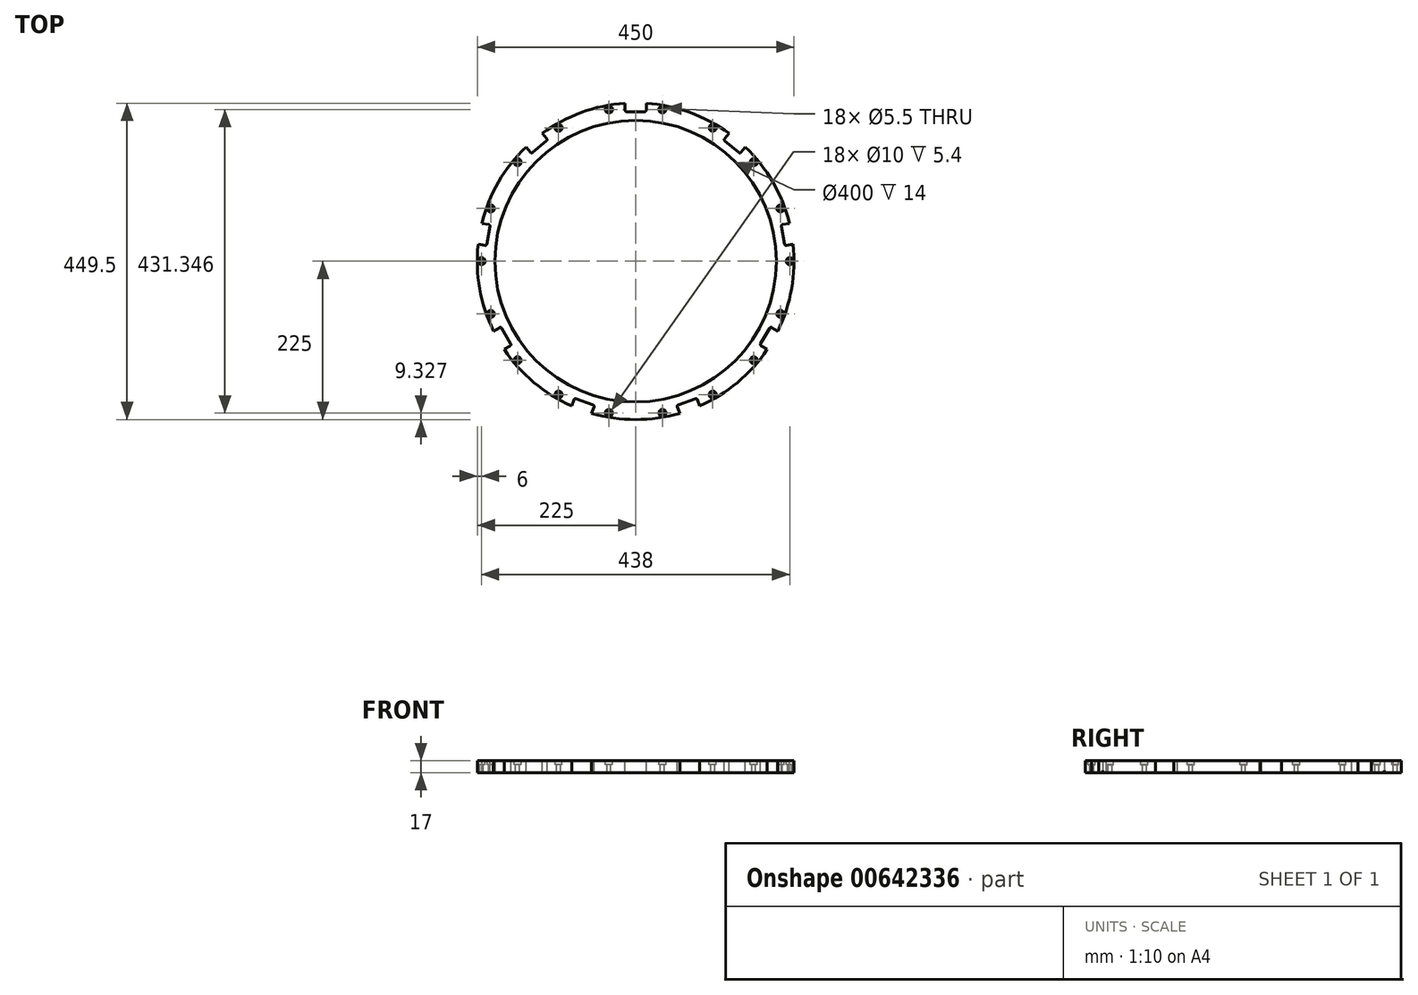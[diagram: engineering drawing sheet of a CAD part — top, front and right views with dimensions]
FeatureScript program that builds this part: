
annotation { "Feature Type Name" : "Feature", "Feature Type Description" : "" }
export const myFeature = defineFeature(function(context is Context, id is Id, definition is map)
    precondition{}
    {
        {
            var Q0;
            Q0=qCreatedBy(makeId("Top.planeOp"),FACE);
            var sketch = newSketch(context, id + "F0", { "sketchPlane" : qUnion([Q0])});
            skCircle(sketch, "E0", {"center": v(0, 0) * mm, "radius": 200 * mm});
            skCircle(sketch, "E1", {"center": v(0, 0) * mm, "radius": 225 * mm});
            skSolve(sketch);
        }
        {
            var Q0;
            Q0=makeQuery(id+"F0.imprint","IMPRINT",FACE,{"disambiguationData":[TD([[makeQuery(id+"F0.imprint","IMPRINT",EDGE,{"derivedFrom":sQuery(id+"F0.wireOp",EDGE,"E0")}),-1.0]])]});
            extrude(context, id + "F1", {"entities" : qUnion([Q0]), "depth" : 17 * mm, "offsetDistance" : 25 * mm});
        }
        {
            var Q0;
            Q0=makeQuery(id+"F1.opExtrude","CAP_FACE",FACE,{"disambiguationData":[OSD([sQuery(id+"F0.wireOp",EDGE,"E0"),sQuery(id+"F0.wireOp",EDGE,"E1")])],"isStart":false});
            var sketch = newSketch(context, id + "F2", { "sketchPlane" : qUnion([Q0])});
            skPoint(sketch, "E2", {"position": v(219, 0) * mm});
            skPoint(sketch, "E3.1.0", {"position": v(205.8, 74.9) * mm});
            skPoint(sketch, "E3.2.0", {"position": v(167.76, 140.77) * mm});
            skPoint(sketch, "E3.3.0", {"position": v(109.5, 189.66) * mm});
            skPoint(sketch, "E3.4.0", {"position": v(38.03, 215.67) * mm});
            skPoint(sketch, "E3.5.0", {"position": v(-38.03, 215.67) * mm});
            skPoint(sketch, "E3.6.0", {"position": v(-109.5, 189.66) * mm});
            skPoint(sketch, "E3.7.0", {"position": v(-167.76, 140.77) * mm});
            skPoint(sketch, "E3.8.0", {"position": v(-205.8, 74.9) * mm});
            skPoint(sketch, "E3.9.0", {"position": v(-219, 0) * mm});
            skPoint(sketch, "E3.10.0", {"position": v(-205.8, -74.9) * mm});
            skPoint(sketch, "E3.11.0", {"position": v(-167.76, -140.77) * mm});
            skPoint(sketch, "E3.12.0", {"position": v(-109.5, -189.66) * mm});
            skPoint(sketch, "E3.13.0", {"position": v(-38.03, -215.67) * mm});
            skPoint(sketch, "E3.14.0", {"position": v(38.03, -215.67) * mm});
            skPoint(sketch, "E3.15.0", {"position": v(109.5, -189.66) * mm});
            skPoint(sketch, "E3.16.0", {"position": v(167.76, -140.77) * mm});
            skPoint(sketch, "E3.17.0", {"position": v(205.8, -74.9) * mm});
            skPoint(sketch, "E3.center", {"position": v(0, 0) * mm});
            skSolve(sketch);
        }
        {
            var Q0;
            Q0=sQuery(id+"F2.wireOp",VERTEX,"E2");
            var Q1;
            Q1=sQuery(id+"F2.wireOp",VERTEX,"E3.1.0");
            var Q2;
            Q2=sQuery(id+"F2.wireOp",VERTEX,"E3.2.0");
            var Q3;
            Q3=sQuery(id+"F2.wireOp",VERTEX,"E3.3.0");
            var Q4;
            Q4=sQuery(id+"F2.wireOp",VERTEX,"E3.4.0");
            var Q5;
            Q5=sQuery(id+"F2.wireOp",VERTEX,"E3.5.0");
            var Q6;
            Q6=sQuery(id+"F2.wireOp",VERTEX,"E3.6.0");
            var Q7;
            Q7=sQuery(id+"F2.wireOp",VERTEX,"E3.7.0");
            var Q8;
            Q8=sQuery(id+"F2.wireOp",VERTEX,"E3.8.0");
            var Q9;
            Q9=sQuery(id+"F2.wireOp",VERTEX,"E3.9.0");
            var Q10;
            Q10=sQuery(id+"F2.wireOp",VERTEX,"E3.10.0");
            var Q11;
            Q11=sQuery(id+"F2.wireOp",VERTEX,"E3.11.0");
            var Q12;
            Q12=sQuery(id+"F2.wireOp",VERTEX,"E3.12.0");
            var Q13;
            Q13=sQuery(id+"F2.wireOp",VERTEX,"E3.13.0");
            var Q14;
            Q14=sQuery(id+"F2.wireOp",VERTEX,"E3.14.0");
            var Q15;
            Q15=sQuery(id+"F2.wireOp",VERTEX,"E3.15.0");
            var Q16;
            Q16=sQuery(id+"F2.wireOp",VERTEX,"E3.16.0");
            var Q17;
            Q17=sQuery(id+"F2.wireOp",VERTEX,"E3.17.0");
            var Q18;
            Q18=sQuery(id+"F2.wireOp",VERTEX,"E3.18.0");
            var Q19;
            Q19=sQuery(id+"F2.wireOp",VERTEX,"E3.19.0");
            var Q20;
            Q20=sQuery(id+"F2.wireOp",VERTEX,"E3.20.0");
            var Q21;
            Q21=sQuery(id+"F2.wireOp",VERTEX,"E3.21.0");
            var Q22;
            Q22=sQuery(id+"F2.wireOp",VERTEX,"E3.22.0");
            var Q23;
            Q23=sQuery(id+"F2.wireOp",VERTEX,"E3.23.0");
            var Q24;
            Q24=sQuery(id+"F2.wireOp",VERTEX,"E3.24.0");
            var Q25;
            Q25=sQuery(id+"F2.wireOp",VERTEX,"E3.25.0");
            var Q26;
            Q26=sQuery(id+"F2.wireOp",VERTEX,"E3.26.0");
            var Q27;
            Q27=sQuery(id+"F2.wireOp",VERTEX,"E3.27.0");
            var Q28;
            Q28=sQuery(id+"F2.wireOp",VERTEX,"E3.28.0");
            var Q29;
            Q29=sQuery(id+"F2.wireOp",VERTEX,"E3.29.0");
            var Q30;
            Q30=sQuery(id+"F2.wireOp",VERTEX,"E3.30.0");
            var Q31;
            Q31=sQuery(id+"F2.wireOp",VERTEX,"E3.31.0");
            var Q32;
            Q32=sQuery(id+"F2.wireOp",VERTEX,"E3.32.0");
            var Q33;
            Q33=sQuery(id+"F2.wireOp",VERTEX,"E3.33.0");
            var Q34;
            Q34=sQuery(id+"F2.wireOp",VERTEX,"E3.34.0");
            var Q35;
            Q35=sQuery(id+"F2.wireOp",VERTEX,"E3.35.0");
            var Q36;
            Q36=makeQuery(id+"F1.opExtrude","SWEPT_BODY",BODY,{"disambiguationData":[OSD([sQuery(id+"F0.wireOp",EDGE,"E0"),sQuery(id+"F0.wireOp",EDGE,"E1")])]});
            hole(context, id + "F3", {"style" : HoleStyle.C_BORE, "endStyle" : HoleEndStyle.THROUGH, "holeDiameter" : 5.5 * mm, "cBoreDiameter" : 10 * mm, "cBoreDepth" : 5.4 * mm, "majorDiameter" : 5 * mm, "isTappedThrough" : true, "tappedDepth" : 12 * mm, "tapClearance" : 3, "locations" : qUnion([Q0, Q1, Q2, Q3, Q4, Q5, Q6, Q7, Q8, Q9, Q10, Q11, Q12, Q13, Q14, Q15, Q16, Q17, Q18, Q19, Q20, Q21, Q22, Q23, Q24, Q25, Q26, Q27, Q28, Q29, Q30, Q31, Q32, Q33, Q34, Q35]), "scope" : qUnion([Q36])});
        }
        {
            var Q0;
            Q0=makeQuery(id+"F1.opExtrude","CAP_EDGE",EDGE,{"disambiguationData":[OSD([sQuery(id+"F0.wireOp",EDGE,"E0")])],"isStart":true});
            fillet(context, id + "F4", {"entities" : qUnion([Q0]), "radius" : 3 * mm, "tangentPropagation" : true, "allowEdgeOverflow" : false});
        }
        {
            var Q0;
            Q0=makeQuery(id+"F1.opExtrude","CAP_FACE",FACE,{"disambiguationData":[OSD([sQuery(id+"F0.wireOp",EDGE,"E0"),sQuery(id+"F0.wireOp",EDGE,"E1")])],"isStart":false});
            var sketch = newSketch(context, id + "F5", { "sketchPlane" : qUnion([Q0])});
            skLineSegment(sketch, "E4", {"start": v(0, 0) * mm, "end": v(221.58, 39.07) * mm, "construction": true});
            skLineSegment(sketch, "E5", {"start": v(218.48, 53.76) * mm, "end": v(208.64, 52.02) * mm});
            skLineSegment(sketch, "E6", {"start": v(207.01, 49.7) * mm, "end": v(209.27, 36.9) * mm});
            skLineSegment(sketch, "E7", {"start": v(209.27, 36.9) * mm, "end": v(211.53, 24.1) * mm});
            skLineSegment(sketch, "E8", {"start": v(213.85, 22.48) * mm, "end": v(223.7, 24.21) * mm});
            skPoint(sketch, "E9.center", {"position": v(0, 0) * mm});
            skPoint(sketch, "E10.visualSharp", {"position": v(206.67, 51.67) * mm});
            skArc(sketch, "E10.filletArc", {"start": v(208.64, 52.02) * mm, "mid": v(207.34, 51.2) * mm, "end": v(207.01, 49.7) * mm});
            skPoint(sketch, "E11.visualSharp", {"position": v(211.88, 22.13) * mm});
            skArc(sketch, "E11.filletArc", {"start": v(211.53, 24.1) * mm, "mid": v(212.35, 22.8) * mm, "end": v(213.85, 22.48) * mm});
            skLineSegment(sketch, "E12.1.0", {"start": v(0, 0) * mm, "end": v(144.63, 172.36) * mm, "construction": true});
            skLineSegment(sketch, "E12.1.1", {"start": v(149.37, 154.67) * mm, "end": v(155.8, 162.33) * mm});
            skLineSegment(sketch, "E12.1.2", {"start": v(132.81, 181.62) * mm, "end": v(126.39, 173.96) * mm});
            skLineSegment(sketch, "E12.1.3", {"start": v(136.6, 162.78) * mm, "end": v(146.55, 154.43) * mm});
            skLineSegment(sketch, "E12.1.4", {"start": v(126.63, 171.14) * mm, "end": v(136.6, 162.78) * mm});
            skPoint(sketch, "E12.1.5", {"position": v(148.08, 153.14) * mm});
            skPoint(sketch, "E12.1.6", {"position": v(125.1, 172.43) * mm});
            skArc(sketch, "E12.1.7", {"start": v(126.39, 173.96) * mm, "mid": v(125.93, 172.5) * mm, "end": v(126.63, 171.14) * mm});
            skArc(sketch, "E12.1.8", {"start": v(146.55, 154.43) * mm, "mid": v(148.01, 153.97) * mm, "end": v(149.37, 154.67) * mm});
            skLineSegment(sketch, "E12.2.0", {"start": v(0, 0) * mm, "end": v(0, 225) * mm, "construction": true});
            skLineSegment(sketch, "E12.2.1", {"start": v(15, 214.5) * mm, "end": v(15, 224.5) * mm});
            skLineSegment(sketch, "E12.2.2", {"start": v(-15, 224.5) * mm, "end": v(-15, 214.5) * mm});
            skLineSegment(sketch, "E12.2.3", {"start": v(0, 212.5) * mm, "end": v(13, 212.5) * mm});
            skLineSegment(sketch, "E12.2.4", {"start": v(-13, 212.5) * mm, "end": v(0, 212.5) * mm});
            skPoint(sketch, "E12.2.5", {"position": v(15, 212.5) * mm});
            skPoint(sketch, "E12.2.6", {"position": v(-15, 212.5) * mm});
            skArc(sketch, "E12.2.7", {"start": v(-15, 214.5) * mm, "mid": v(-14.41, 213.09) * mm, "end": v(-13, 212.5) * mm});
            skArc(sketch, "E12.2.8", {"start": v(13, 212.5) * mm, "mid": v(14.41, 213.09) * mm, "end": v(15, 214.5) * mm});
            skLineSegment(sketch, "E12.3.0", {"start": v(0, 0) * mm, "end": v(-144.63, 172.36) * mm, "construction": true});
            skLineSegment(sketch, "E12.3.1", {"start": v(-126.39, 173.96) * mm, "end": v(-132.81, 181.62) * mm});
            skLineSegment(sketch, "E12.3.2", {"start": v(-155.8, 162.33) * mm, "end": v(-149.37, 154.67) * mm});
            skLineSegment(sketch, "E12.3.3", {"start": v(-136.6, 162.78) * mm, "end": v(-126.63, 171.14) * mm});
            skLineSegment(sketch, "E12.3.4", {"start": v(-146.55, 154.43) * mm, "end": v(-136.6, 162.78) * mm});
            skPoint(sketch, "E12.3.5", {"position": v(-125.1, 172.43) * mm});
            skPoint(sketch, "E12.3.6", {"position": v(-148.08, 153.14) * mm});
            skArc(sketch, "E12.3.7", {"start": v(-149.37, 154.67) * mm, "mid": v(-148.01, 153.97) * mm, "end": v(-146.55, 154.43) * mm});
            skArc(sketch, "E12.3.8", {"start": v(-126.63, 171.14) * mm, "mid": v(-125.93, 172.5) * mm, "end": v(-126.39, 173.96) * mm});
            skLineSegment(sketch, "E12.4.0", {"start": v(0, 0) * mm, "end": v(-221.58, 39.07) * mm, "construction": true});
            skLineSegment(sketch, "E12.4.1", {"start": v(-208.64, 52.02) * mm, "end": v(-218.48, 53.76) * mm});
            skLineSegment(sketch, "E12.4.2", {"start": v(-223.7, 24.21) * mm, "end": v(-213.85, 22.48) * mm});
            skLineSegment(sketch, "E12.4.3", {"start": v(-209.27, 36.9) * mm, "end": v(-207.01, 49.7) * mm});
            skLineSegment(sketch, "E12.4.4", {"start": v(-211.53, 24.1) * mm, "end": v(-209.27, 36.9) * mm});
            skPoint(sketch, "E12.4.5", {"position": v(-206.67, 51.67) * mm});
            skPoint(sketch, "E12.4.6", {"position": v(-211.88, 22.13) * mm});
            skArc(sketch, "E12.4.7", {"start": v(-213.85, 22.48) * mm, "mid": v(-212.35, 22.8) * mm, "end": v(-211.53, 24.1) * mm});
            skArc(sketch, "E12.4.8", {"start": v(-207.01, 49.7) * mm, "mid": v(-207.34, 51.2) * mm, "end": v(-208.64, 52.02) * mm});
            skLineSegment(sketch, "E12.5.0", {"start": v(0, 0) * mm, "end": v(-194.86, -112.5) * mm, "construction": true});
            skLineSegment(sketch, "E12.5.1", {"start": v(-193.26, -94.26) * mm, "end": v(-201.92, -99.26) * mm});
            skLineSegment(sketch, "E12.5.2", {"start": v(-186.92, -125.24) * mm, "end": v(-178.26, -120.24) * mm});
            skLineSegment(sketch, "E12.5.3", {"start": v(-184.03, -106.25) * mm, "end": v(-190.53, -95) * mm});
            skLineSegment(sketch, "E12.5.4", {"start": v(-177.53, -117.5) * mm, "end": v(-184.03, -106.25) * mm});
            skPoint(sketch, "E12.5.5", {"position": v(-191.53, -93.26) * mm});
            skPoint(sketch, "E12.5.6", {"position": v(-176.53, -119.24) * mm});
            skArc(sketch, "E12.5.7", {"start": v(-178.26, -120.24) * mm, "mid": v(-177.33, -119.03) * mm, "end": v(-177.53, -117.5) * mm});
            skArc(sketch, "E12.5.8", {"start": v(-190.53, -95) * mm, "mid": v(-191.74, -94.06) * mm, "end": v(-193.26, -94.26) * mm});
            skLineSegment(sketch, "E12.6.0", {"start": v(0, 0) * mm, "end": v(-76.95, -211.43) * mm, "construction": true});
            skLineSegment(sketch, "E12.6.1", {"start": v(-87.46, -196.43) * mm, "end": v(-90.88, -205.83) * mm});
            skLineSegment(sketch, "E12.6.2", {"start": v(-62.69, -216.1) * mm, "end": v(-59.27, -206.7) * mm});
            skLineSegment(sketch, "E12.6.3", {"start": v(-72.68, -199.68) * mm, "end": v(-84.9, -195.24) * mm});
            skLineSegment(sketch, "E12.6.4", {"start": v(-60.46, -204.13) * mm, "end": v(-72.68, -199.68) * mm});
            skPoint(sketch, "E12.6.5", {"position": v(-86.77, -194.55) * mm});
            skPoint(sketch, "E12.6.6", {"position": v(-58.58, -204.81) * mm});
            skArc(sketch, "E12.6.7", {"start": v(-59.27, -206.7) * mm, "mid": v(-59.33, -205.16) * mm, "end": v(-60.46, -204.13) * mm});
            skArc(sketch, "E12.6.8", {"start": v(-84.9, -195.24) * mm, "mid": v(-86.42, -195.3) * mm, "end": v(-87.46, -196.43) * mm});
            skLineSegment(sketch, "E12.7.0", {"start": v(0, 0) * mm, "end": v(76.95, -211.43) * mm, "construction": true});
            skLineSegment(sketch, "E12.7.1", {"start": v(59.27, -206.7) * mm, "end": v(62.69, -216.1) * mm});
            skLineSegment(sketch, "E12.7.2", {"start": v(90.88, -205.83) * mm, "end": v(87.46, -196.43) * mm});
            skLineSegment(sketch, "E12.7.3", {"start": v(72.68, -199.68) * mm, "end": v(60.46, -204.13) * mm});
            skLineSegment(sketch, "E12.7.4", {"start": v(84.9, -195.24) * mm, "end": v(72.68, -199.68) * mm});
            skPoint(sketch, "E12.7.5", {"position": v(58.58, -204.81) * mm});
            skPoint(sketch, "E12.7.6", {"position": v(86.77, -194.55) * mm});
            skArc(sketch, "E12.7.7", {"start": v(87.46, -196.43) * mm, "mid": v(86.42, -195.3) * mm, "end": v(84.9, -195.24) * mm});
            skArc(sketch, "E12.7.8", {"start": v(60.46, -204.13) * mm, "mid": v(59.33, -205.16) * mm, "end": v(59.27, -206.7) * mm});
            skLineSegment(sketch, "E12.8.0", {"start": v(0, 0) * mm, "end": v(194.86, -112.5) * mm, "construction": true});
            skLineSegment(sketch, "E12.8.1", {"start": v(178.26, -120.24) * mm, "end": v(186.92, -125.24) * mm});
            skLineSegment(sketch, "E12.8.2", {"start": v(201.92, -99.26) * mm, "end": v(193.26, -94.26) * mm});
            skLineSegment(sketch, "E12.8.3", {"start": v(184.03, -106.25) * mm, "end": v(177.53, -117.5) * mm});
            skLineSegment(sketch, "E12.8.4", {"start": v(190.53, -95) * mm, "end": v(184.03, -106.25) * mm});
            skPoint(sketch, "E12.8.5", {"position": v(176.53, -119.24) * mm});
            skPoint(sketch, "E12.8.6", {"position": v(191.53, -93.26) * mm});
            skArc(sketch, "E12.8.7", {"start": v(193.26, -94.26) * mm, "mid": v(191.74, -94.06) * mm, "end": v(190.53, -95) * mm});
            skArc(sketch, "E12.8.8", {"start": v(177.53, -117.5) * mm, "mid": v(177.33, -119.03) * mm, "end": v(178.26, -120.24) * mm});
            skSolve(sketch);
        }
        {
            var Q0;
            {var subQ1=sQuery(id+"F5.wireOp",EDGE,"E5");Q0=makeQuery(id+"F5.imprint","IMPRINT",FACE,{"disambiguationData":[TD([[makeQuery(id+"F5.imprint","IMPRINT",EDGE,{"derivedFrom":subQ1}),1.0]])]});}
            var Q1;
            {var subQ1=sQuery(id+"F5.wireOp",EDGE,"E12.1.1");Q1=makeQuery(id+"F5.imprint","IMPRINT",FACE,{"disambiguationData":[TD([[makeQuery(id+"F5.imprint","IMPRINT",EDGE,{"derivedFrom":subQ1}),1.0]])]});}
            var Q2;
            {var subQ1=sQuery(id+"F5.wireOp",EDGE,"E12.2.1");Q2=makeQuery(id+"F5.imprint","IMPRINT",FACE,{"disambiguationData":[TD([[makeQuery(id+"F5.imprint","IMPRINT",EDGE,{"derivedFrom":subQ1}),1.0]])]});}
            var Q3;
            {var subQ1=sQuery(id+"F5.wireOp",EDGE,"E12.3.1");Q3=makeQuery(id+"F5.imprint","IMPRINT",FACE,{"disambiguationData":[TD([[makeQuery(id+"F5.imprint","IMPRINT",EDGE,{"derivedFrom":subQ1}),1.0]])]});}
            var Q4;
            {var subQ0=sQuery(id+"F5.wireOp",EDGE,"E12.4.1");Q4=makeQuery(id+"F5.imprint","IMPRINT",FACE,{"disambiguationData":[TD([[makeQuery(id+"F5.imprint","IMPRINT",EDGE,{"derivedFrom":subQ0}),1.0]])]});}
            var Q5;
            {var subQ1=sQuery(id+"F5.wireOp",EDGE,"E12.5.1");Q5=makeQuery(id+"F5.imprint","IMPRINT",FACE,{"disambiguationData":[TD([[makeQuery(id+"F5.imprint","IMPRINT",EDGE,{"derivedFrom":subQ1}),1.0]])]});}
            var Q6;
            {var subQ1=sQuery(id+"F5.wireOp",EDGE,"E12.6.1");Q6=makeQuery(id+"F5.imprint","IMPRINT",FACE,{"disambiguationData":[TD([[makeQuery(id+"F5.imprint","IMPRINT",EDGE,{"derivedFrom":subQ1}),1.0]])]});}
            var Q7;
            {var subQ0=sQuery(id+"F5.wireOp",EDGE,"E12.7.1");Q7=makeQuery(id+"F5.imprint","IMPRINT",FACE,{"disambiguationData":[TD([[makeQuery(id+"F5.imprint","IMPRINT",EDGE,{"derivedFrom":subQ0}),1.0]])]});}
            var Q8;
            {var subQ1=sQuery(id+"F5.wireOp",EDGE,"E12.8.1");Q8=makeQuery(id+"F5.imprint","IMPRINT",FACE,{"disambiguationData":[TD([[makeQuery(id+"F5.imprint","IMPRINT",EDGE,{"derivedFrom":subQ1}),1.0]])]});}
            extrude(context, id + "F6", {"entities" : qUnion([Q0, Q1, Q2, Q3, Q4, Q5, Q6, Q7, Q8]), "operationType" : NewBodyOperationType.REMOVE, "endBound" : BoundingType.THROUGH_ALL, "oppositeDirection" : true, "depth" : 25 * mm, "offsetDistance" : 25 * mm});
        }
    });
